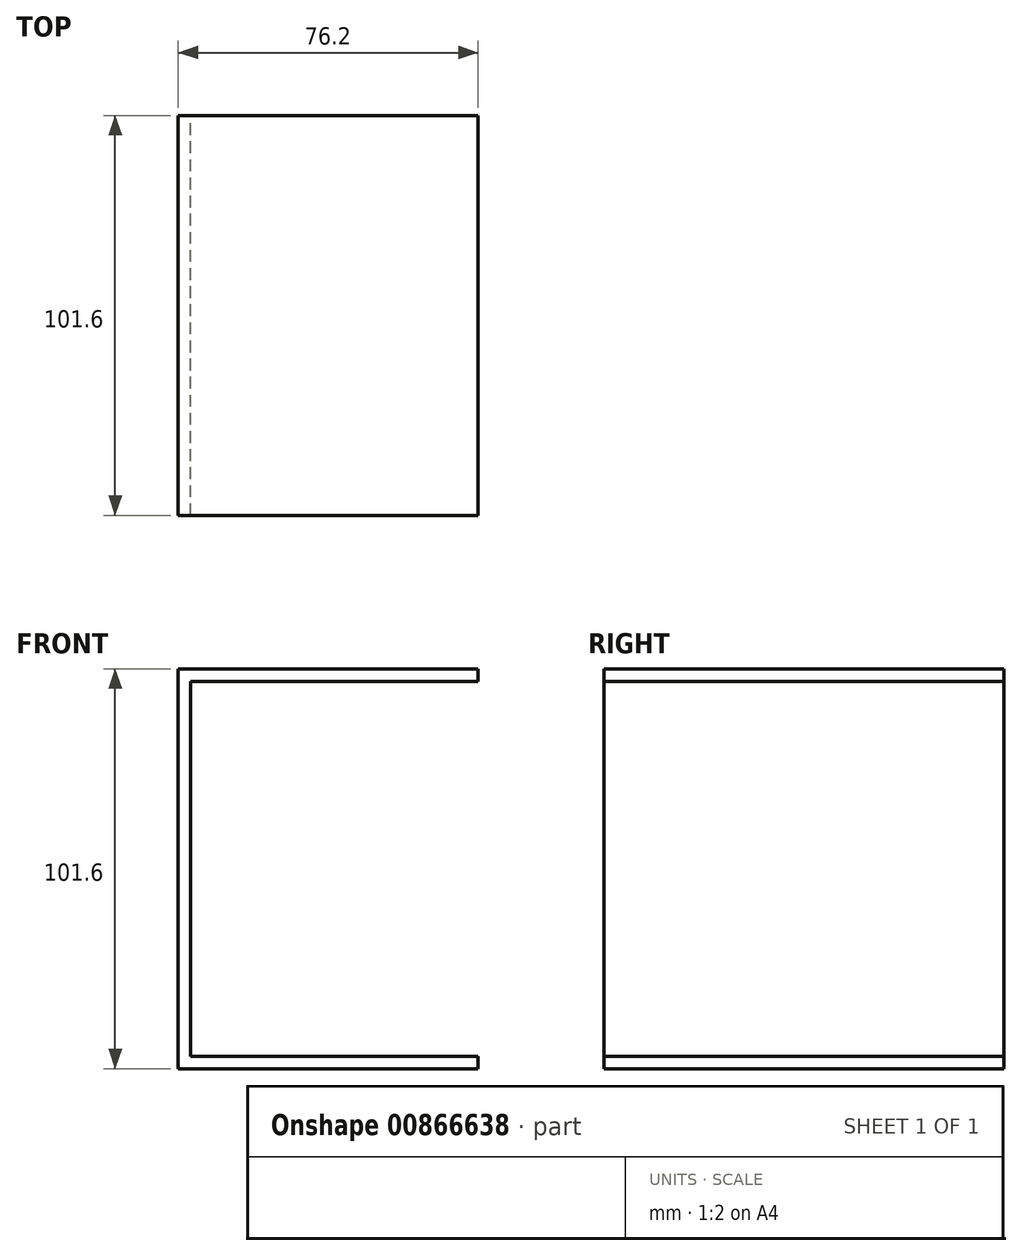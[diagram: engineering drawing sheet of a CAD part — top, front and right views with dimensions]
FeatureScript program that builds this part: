
annotation { "Feature Type Name" : "Feature", "Feature Type Description" : "" }
export const myFeature = defineFeature(function(context is Context, id is Id, definition is map)
    precondition{}
    {
        {
            var Q0;
            Q0=qCreatedBy(makeId("Front.planeOp"),FACE);
            var sketch = newSketch(context, id + "F0", { "sketchPlane" : qUnion([Q0])});
            skLineSegment(sketch, "E0.bottom", {"start": v(38.1, -50.8) * mm, "end": v(-38.1, -50.8) * mm});
            skLineSegment(sketch, "E0.top", {"start": v(38.1, 50.8) * mm, "end": v(-38.1, 50.8) * mm});
            skLineSegment(sketch, "E0.left", {"start": v(38.1, -50.8) * mm, "end": v(38.1, -47.62) * mm});
            skLineSegment(sketch, "E0.right", {"start": v(-38.1, -50.8) * mm, "end": v(-38.1, 50.8) * mm});
            skPoint(sketch, "E0.middle", {"position": v(0, 0) * mm});
            skLineSegment(sketch, "E1.bottom", {"start": v(38.1, 47.63) * mm, "end": v(-34.92, 47.63) * mm});
            skLineSegment(sketch, "E1.top", {"start": v(38.1, -47.63) * mm, "end": v(-34.92, -47.63) * mm});
            skLineSegment(sketch, "E1.right", {"start": v(-34.93, 47.62) * mm, "end": v(-34.92, -47.63) * mm});
            skLineSegment(sketch, "E2", {"start": v(0, 47.63) * mm, "end": v(0, 50.8) * mm, "construction": true});
            skPoint(sketch, "E2.startSnap0", {"position": v(0, 50.8) * mm});
            skLineSegment(sketch, "E3", {"start": v(0, -50.8) * mm, "end": v(0, -47.63) * mm, "construction": true});
            skLineSegment(sketch, "E4", {"start": v(-38.1, 0) * mm, "end": v(-34.93, 0) * mm, "construction": true});
            skLineSegment(sketch, "E5.trimOffspring", {"start": v(38.1, 47.63) * mm, "end": v(38.1, 50.8) * mm});
            skSolve(sketch);
        }
        {
            var Q0;
            Q0 = qSketchRegion(id + "F0", true);
            extrude(context, id + "F1", {"entities" : qUnion([Q0]), "endBound" : BoundingType.SYMMETRIC, "depth" : 101.6 * mm, "offsetDistance" : 25.4 * mm});
        }
    });
